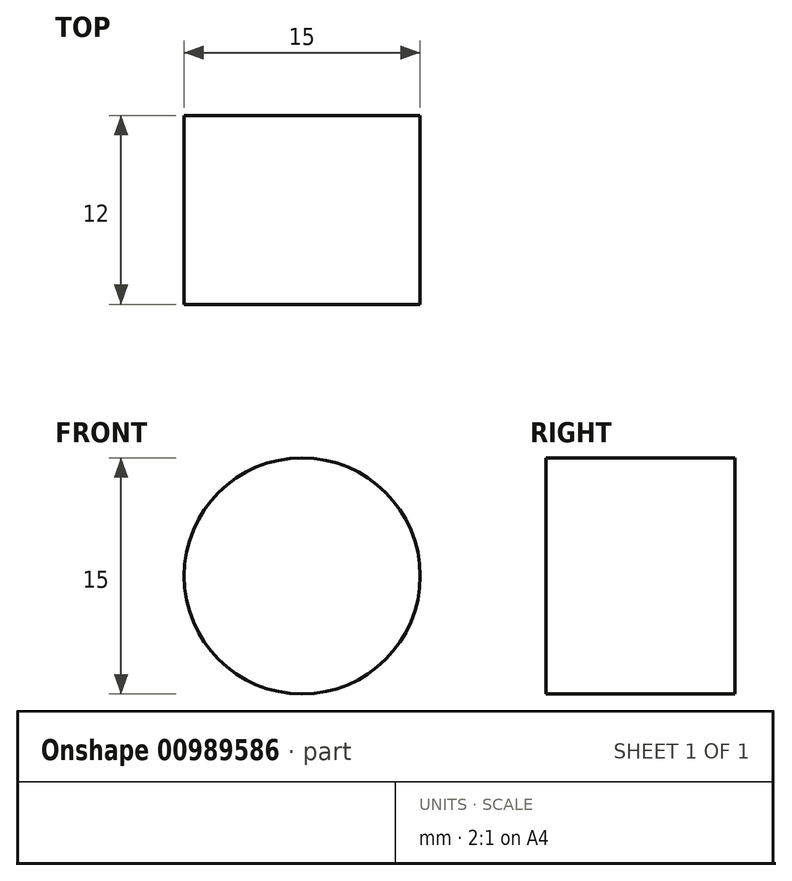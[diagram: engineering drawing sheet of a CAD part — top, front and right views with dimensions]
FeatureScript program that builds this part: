
annotation { "Feature Type Name" : "Feature", "Feature Type Description" : "" }
export const myFeature = defineFeature(function(context is Context, id is Id, definition is map)
    precondition{}
    {
        {
            var Q0;
            Q0=qCreatedBy(makeId("Front.planeOp"),FACE);
            var sketch = newSketch(context, id + "F0", { "sketchPlane" : qUnion([Q0])});
            skCircle(sketch, "E0", {"center": v(0, 0) * mm, "radius": 7.5 * mm});
            skSolve(sketch);
        }
        {
            var Q0;
            Q0=makeQuery(id+"F0.imprint","IMPRINT",FACE,{"disambiguationData":[TD([[makeQuery(id+"F0.imprint","IMPRINT",EDGE,{"derivedFrom":sQuery(id+"F0.wireOp",EDGE,"E0")}),1.0]])]});
            extrude(context, id + "F1", {"entities" : qUnion([Q0]), "oppositeDirection" : true, "depth" : 12 * mm, "offsetDistance" : 25 * mm});
        }
    });
